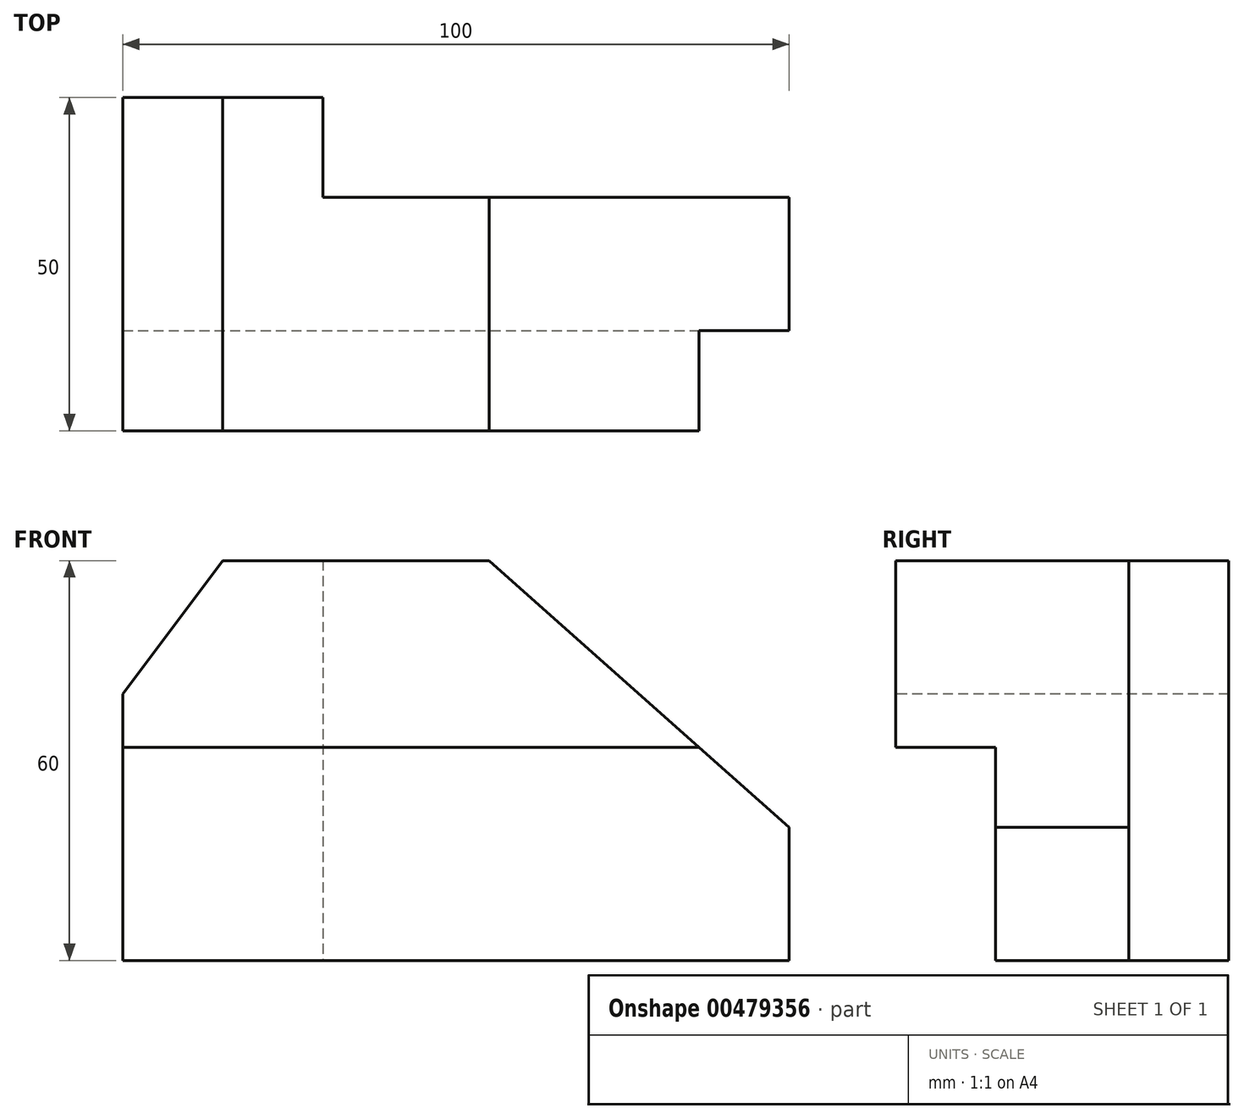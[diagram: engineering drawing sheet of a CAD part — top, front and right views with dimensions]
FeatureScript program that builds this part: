
annotation { "Feature Type Name" : "Feature", "Feature Type Description" : "" }
export const myFeature = defineFeature(function(context is Context, id is Id, definition is map)
    precondition{}
    {
        {
            var Q0;
            Q0=qCreatedBy(makeId("Top.planeOp"),FACE);
            var sketch = newSketch(context, id + "F0", { "sketchPlane" : qUnion([Q0])});
            skLineSegment(sketch, "E0.bottom", {"start": v(0, 0) * mm, "end": v(100, 0) * mm});
            skLineSegment(sketch, "E0.top", {"start": v(0, 50) * mm, "end": v(100, 50) * mm});
            skLineSegment(sketch, "E0.left", {"start": v(0, 0) * mm, "end": v(0, 50) * mm});
            skLineSegment(sketch, "E0.right", {"start": v(100, 0) * mm, "end": v(100, 50) * mm});
            skSolve(sketch);
        }
        {
            var Q0;
            Q0 = qSketchRegion(id + "F0", true);
            extrude(context, id + "F1", {"entities" : qUnion([Q0]), "depth" : 60 * mm});
        }
        {
            var Q0;
            Q0=makeQuery(id+"F1.opExtrude","SWEPT_FACE",FACE,{"disambiguationData":[OSD([sQuery(id+"F0.wireOp",EDGE,"E0.bottom")])]});
            var sketch = newSketch(context, id + "F2", { "sketchPlane" : qUnion([Q0])});
            skLineSegment(sketch, "E1", {"start": v(0, 0) * mm, "end": v(0, 40) * mm});
            skLineSegment(sketch, "E2", {"start": v(0, 60) * mm, "end": v(15, 60) * mm});
            skLineSegment(sketch, "E3", {"start": v(15, 60) * mm, "end": v(0, 40) * mm});
            skLineSegment(sketch, "E4", {"start": v(0, 60) * mm, "end": v(0, 40) * mm});
            skLineSegment(sketch, "E5", {"start": v(0, 60) * mm, "end": v(55, 60) * mm});
            skLineSegment(sketch, "E6", {"start": v(100, 0) * mm, "end": v(100, 20) * mm});
            skLineSegment(sketch, "E7", {"start": v(55, 60) * mm, "end": v(100, 20) * mm});
            skSolve(sketch);
        }
        {
            var Q0;
            Q0 = qSketchRegion(id + "F2", true);
            var Q1;
            {var subQ0=sQuery(id+"F2.wireOp",EDGE,"E7");Q1=makeQuery(id+"F2.imprint","IMPRINT",FACE,{"disambiguationData":[TD([[makeQuery(id+"F2.imprint","IMPRINT",EDGE,{"derivedFrom":subQ0}),1.0]])]});}
            extrude(context, id + "F3", {"entities" : qUnion([Q0, Q1]), "operationType" : NewBodyOperationType.REMOVE, "endBound" : BoundingType.THROUGH_ALL, "oppositeDirection" : true, "depth" : 25 * mm});
        }
        {
            var Q0;
            Q0=makeQuery(id+"F1.opExtrude","SWEPT_FACE",FACE,{"disambiguationData":[OSD([sQuery(id+"F0.wireOp",EDGE,"E0.bottom")])]});
            var sketch = newSketch(context, id + "F4", { "sketchPlane" : qUnion([Q0])});
            skLineSegment(sketch, "E8.bottom", {"start": v(0, 0) * mm, "end": v(100, 0) * mm});
            skLineSegment(sketch, "E8.top", {"start": v(0, 32) * mm, "end": v(100, 32) * mm});
            skLineSegment(sketch, "E8.left", {"start": v(0, 0) * mm, "end": v(0, 32) * mm});
            skLineSegment(sketch, "E8.right", {"start": v(100, 0) * mm, "end": v(100, 32) * mm});
            skSolve(sketch);
        }
        {
            var Q0;
            Q0 = qSketchRegion(id + "F4", true);
            extrude(context, id + "F5", {"entities" : qUnion([Q0]), "operationType" : NewBodyOperationType.REMOVE, "oppositeDirection" : true, "depth" : 15 * mm});
        }
        {
            var Q0;
            Q0=makeQuery(id+"F1.opExtrude","CAP_FACE",FACE,{"disambiguationData":[OSD([sQuery(id+"F0.wireOp",EDGE,"E0.bottom"),sQuery(id+"F0.wireOp",EDGE,"E0.top"),sQuery(id+"F0.wireOp",EDGE,"E0.left"),sQuery(id+"F0.wireOp",EDGE,"E0.right")])],"isStart":true});
            var sketch = newSketch(context, id + "F6", { "sketchPlane" : qUnion([Q0])});
            skLineSegment(sketch, "E9.bottom", {"start": v(0, -50) * mm, "end": v(30, -50) * mm});
            skLineSegment(sketch, "E9.top", {"start": v(0, -35) * mm, "end": v(30, -35) * mm});
            skLineSegment(sketch, "E9.left", {"start": v(0, -50) * mm, "end": v(0, -35) * mm});
            skLineSegment(sketch, "E9.right", {"start": v(30, -50) * mm, "end": v(30, -35) * mm});
            skLineSegment(sketch, "E10.bottom", {"start": v(30, -35) * mm, "end": v(100, -35) * mm});
            skLineSegment(sketch, "E10.top", {"start": v(30, -50) * mm, "end": v(100, -50) * mm});
            skLineSegment(sketch, "E10.left", {"start": v(30, -35) * mm, "end": v(30, -50) * mm});
            skLineSegment(sketch, "E10.right", {"start": v(100, -35) * mm, "end": v(100, -50) * mm});
            skSolve(sketch);
        }
        {
            var Q0;
            Q0=makeQuery(id+"F6.imprint","IMPRINT",FACE,{"disambiguationData":[TD([[makeQuery(id+"F6.imprint","IMPRINT",EDGE,{"derivedFrom":sQuery(id+"F6.wireOp",EDGE,"E10.bottom")}),-1.0]])]});
            extrude(context, id + "F7", {"entities" : qUnion([Q0]), "operationType" : NewBodyOperationType.REMOVE, "endBound" : BoundingType.THROUGH_ALL, "oppositeDirection" : true, "depth" : 25 * mm});
        }
    });
